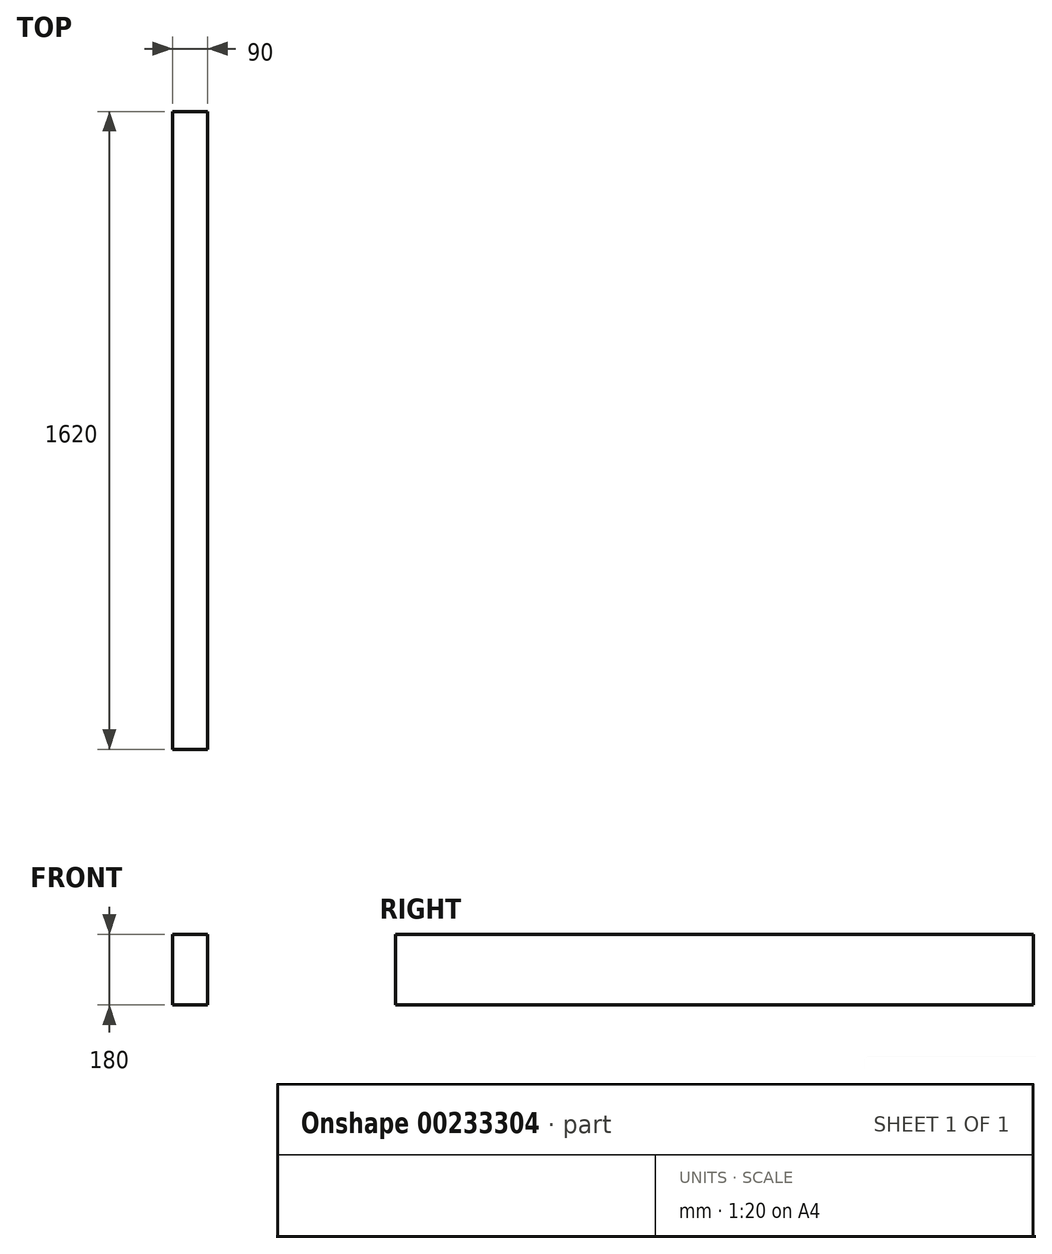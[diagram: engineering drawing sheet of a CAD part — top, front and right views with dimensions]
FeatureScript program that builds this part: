
annotation { "Feature Type Name" : "Feature", "Feature Type Description" : "" }
export const myFeature = defineFeature(function(context is Context, id is Id, definition is map)
    precondition{}
    {
        {
            var Q0;
            Q0=qCreatedBy(makeId("Front.planeOp"),FACE);
            var sketch = newSketch(context, id + "F0", { "sketchPlane" : qUnion([Q0])});
            skLineSegment(sketch, "E0", {"start": v(-53.57, 29.27) * mm, "end": v(-53.57, -150.73) * mm});
            skLineSegment(sketch, "E1", {"start": v(-53.57, -150.73) * mm, "end": v(36.43, -150.73) * mm});
            skLineSegment(sketch, "E2", {"start": v(36.43, -150.73) * mm, "end": v(36.43, 29.27) * mm});
            skLineSegment(sketch, "E3", {"start": v(36.43, 29.27) * mm, "end": v(-53.57, 29.27) * mm});
            skSolve(sketch);
        }
        {
            var Q0;
            Q0 = qSketchRegion(id + "F0", true);
            extrude(context, id + "F1", {"entities" : qUnion([Q0]), "depth" : 1620 * mm});
        }
    });
